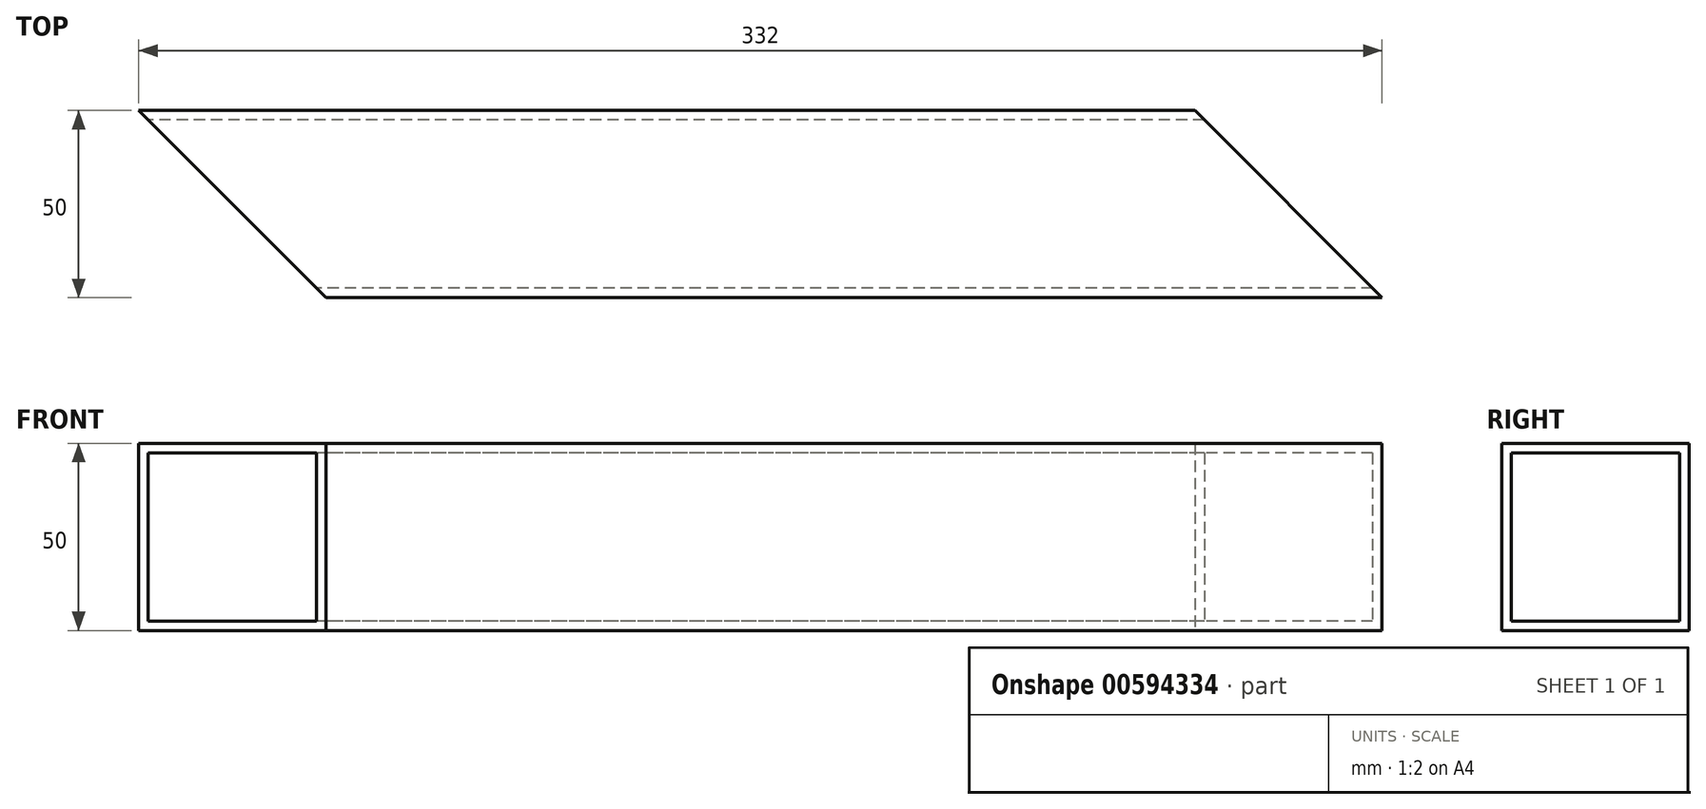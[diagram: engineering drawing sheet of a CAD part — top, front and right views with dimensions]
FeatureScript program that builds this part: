
annotation { "Feature Type Name" : "Feature", "Feature Type Description" : "" }
export const myFeature = defineFeature(function(context is Context, id is Id, definition is map)
    precondition{}
    {
        {
            var Q0;
            Q0=qCreatedBy(makeId("Top.planeOp"),FACE);
            var sketch = newSketch(context, id + "F0", { "sketchPlane" : qUnion([Q0])});
            skLineSegment(sketch, "E0.bottom", {"start": v(116, -25) * mm, "end": v(-116, -25) * mm});
            skLineSegment(sketch, "E0.top", {"start": v(116, 25) * mm, "end": v(-116, 25) * mm});
            skLineSegment(sketch, "E0.left", {"start": v(116, -25) * mm, "end": v(116, 25) * mm});
            skLineSegment(sketch, "E0.right", {"start": v(-116, -25) * mm, "end": v(-116, 25) * mm});
            skPoint(sketch, "E0.middle", {"position": v(0, 0) * mm});
            skLineSegment(sketch, "E1", {"start": v(-116, 25) * mm, "end": v(-166, 25) * mm});
            skLineSegment(sketch, "E2", {"start": v(-166, 25) * mm, "end": v(-116, -25) * mm});
            skLineSegment(sketch, "E3", {"start": v(116, -25) * mm, "end": v(166, -25) * mm});
            skLineSegment(sketch, "E4", {"start": v(166, -25) * mm, "end": v(116, 25) * mm});
            skSolve(sketch);
        }
        {
            var Q0;
            Q0=makeQuery(id+"F0.imprint","IMPRINT",FACE,{"disambiguationData":[TD([[makeQuery(id+"F0.imprint","IMPRINT",EDGE,{"derivedFrom":sQuery(id+"F0.wireOp",EDGE,"E0.bottom")}),-1.0]])]});
            var Q1;
            Q1=makeQuery(id+"F0.imprint","IMPRINT",FACE,{"disambiguationData":[TD([[makeQuery(id+"F0.imprint","IMPRINT",EDGE,{"derivedFrom":sQuery(id+"F0.wireOp",EDGE,"E0.right")}),1.0]])]});
            var Q2;
            Q2=makeQuery(id+"F0.imprint","IMPRINT",FACE,{"disambiguationData":[TD([[makeQuery(id+"F0.imprint","IMPRINT",EDGE,{"derivedFrom":sQuery(id+"F0.wireOp",EDGE,"E0.left")}),-1.0]])]});
            extrude(context, id + "F1", {"entities" : qUnion([Q0, Q1, Q2]), "depth" : 50 * mm, "offsetDistance" : 25.4 * mm});
        }
        {
            var Q0;
            Q0=makeQuery(id+"F1.opExtrude","SWEPT_FACE",FACE,{"disambiguationData":[OSD([sQuery(id+"F0.wireOp",EDGE,"E2")])]});
            var Q1;
            Q1=makeQuery(id+"F1.opExtrude","SWEPT_FACE",FACE,{"disambiguationData":[OSD([sQuery(id+"F0.wireOp",EDGE,"E4")])]});
            shell(context, id + "F2", {"entities" : qUnion([Q0, Q1]), "thickness" : 2.54 * mm});
        }
    });
